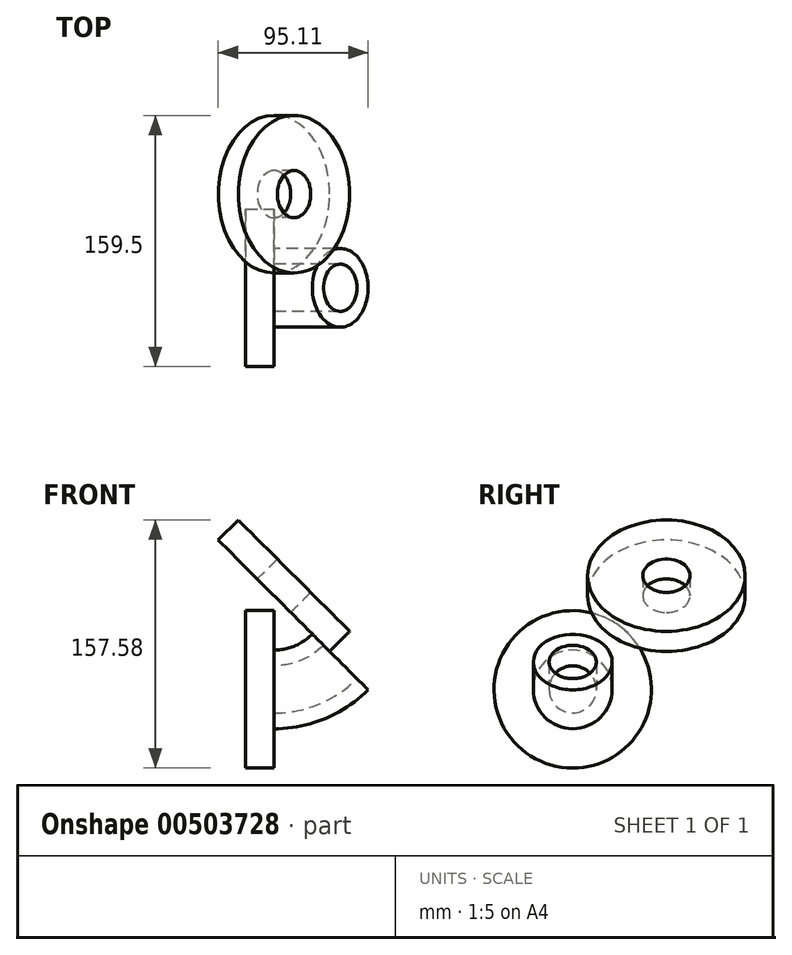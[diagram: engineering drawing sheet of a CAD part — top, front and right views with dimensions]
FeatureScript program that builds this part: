
annotation { "Feature Type Name" : "Feature", "Feature Type Description" : "" }
export const myFeature = defineFeature(function(context is Context, id is Id, definition is map)
    precondition{}
    {
        {
            var Q0;
            Q0=qCreatedBy(makeId("Front.planeOp"),FACE);
            var sketch = newSketch(context, id + "F0", { "sketchPlane" : qUnion([Q0])});
            skArc(sketch, "E0", {"start": v(0, -59.5) * mm, "mid": v(22.77, -54.97) * mm, "end": v(42.07, -42.07) * mm});
            skLineSegment(sketch, "E1", {"start": v(0, 0) * mm, "end": v(0, -59.5) * mm});
            skLineSegment(sketch, "E2", {"start": v(0, -59.5) * mm, "end": v(0, 0) * mm});
            skLineSegment(sketch, "E3", {"start": v(0, 0) * mm, "end": v(42.07, -42.07) * mm});
            skSolve(sketch);
        }
        {
            var Q0;
            Q0=qCreatedBy(makeId("Right.planeOp"),FACE);
            var sketch = newSketch(context, id + "F1", { "sketchPlane" : qUnion([Q0])});
            skLineSegment(sketch, "E4.0", {"start": v(0, -59.5) * mm, "end": v(0, -42.07) * mm});
            skCircle(sketch, "E5", {"center": v(0, -59.5) * mm, "radius": 50 * mm});
            skCircle(sketch, "E6", {"center": v(0, -59.5) * mm, "radius": 15 * mm});
            skCircle(sketch, "E7", {"center": v(0, -59.5) * mm, "radius": 25 * mm});
            skSolve(sketch);
        }
        {
            var Q0;
            Q0 = qSketchRegion(id + "F1", true);
            var Q1;
            Q1=makeQuery(id+"F1.imprint","IMPRINT",FACE,{"disambiguationData":[TD([[makeQuery(id+"F1.imprint","IMPRINT",EDGE,{"derivedFrom":sQuery(id+"F1.wireOp",EDGE,"E6")}),-1.0]])]});
            var Q2;
            Q2=makeQuery(id+"F1.imprint","IMPRINT",FACE,{"disambiguationData":[TD([[makeQuery(id+"F1.imprint","IMPRINT",EDGE,{"derivedFrom":sQuery(id+"F1.wireOp",EDGE,"E6")}),1.0]])]});
            extrude(context, id + "F2", {"entities" : qUnion([Q0, Q1, Q2]), "oppositeDirection" : true, "depth" : 18 * mm});
        }
        {
            var Q0;
            Q0=makeQuery(id+"F1.imprint","IMPRINT",FACE,{"disambiguationData":[TD([[makeQuery(id+"F1.imprint","IMPRINT",EDGE,{"derivedFrom":sQuery(id+"F1.wireOp",EDGE,"E6")}),-1.0]])]});
            var Q1;
            Q1=sQuery(id+"F0.wireOp",EDGE,"E0");
            sweep(context, id + "F3", {"operationType" : NewBodyOperationType.ADD, "profiles" : qUnion([Q0]), "path" : qUnion([Q1])});
        }
        {
            var Q0;
            Q0=makeQuery(id+"F3.opSweep","CAP_FACE",FACE,{"disambiguationData":[OSD([sQuery(id+"F0.wireOp",VERTEX,"E0.end"),sQuery(id+"F1.wireOp",EDGE,"E6"),sQuery(id+"F1.wireOp",EDGE,"E7")])],"isStart":false});
            var sketch = newSketch(context, id + "F4", { "sketchPlane" : qUnion([Q0])});
            skLineSegment(sketch, "E8", {"start": v(42.07, 15) * mm, "end": v(59.5, 15) * mm});
            skCircle(sketch, "E9.0", {"center": v(59.5, 0) * mm, "radius": 15 * mm});
            skCircle(sketch, "E10", {"center": v(59.5, 0) * mm, "radius": 50 * mm});
            skSolve(sketch);
        }
        {
            var Q0;
            Q0 = qSketchRegion(id + "F4", true);
            extrude(context, id + "F5", {"entities" : qUnion([Q0]), "operationType" : NewBodyOperationType.ADD, "depth" : 18 * mm});
        }
    });
